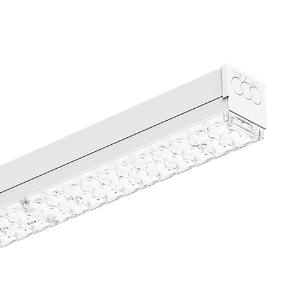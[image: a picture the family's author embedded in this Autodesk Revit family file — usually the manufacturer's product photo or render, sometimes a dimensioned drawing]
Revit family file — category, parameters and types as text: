
# Revit family: 3f_filippi_-_3f_zeta_l_3f_filippi_-_10893_-_3f_zeta_l_30_led_l1194
name_source: partatom
category: Lighting Fixtures
units: mm (PartAtom-declared; Revit-internal decimal feet)

## family parameters
Cut with Voids When Loaded = No
Host = Face
Light Source = No
Part Type = Normal
Room Calculation Point = No
Round Connector Dimension = Use Diameter
Shared = No

## types (1)
- 3F Filippi - 3F Zeta L (1 x LED, 5498 lm, 31 W, 4000 K)
    Apparent Load = 31 VA
    Approval mark = CE
    CIE Flux Codes = 61 95 99 99 100
    Color Rendering = 80
    Color Temperature = 4000 K
    Control Gear = Electronic ballast
    Default Elevation = 1800 mm
    Description = ILLUMINOTECHNICAL
Luminous efficiency 100% (DLOR 99%, ULOR 1%).
Initial luminous flux of the luminaire 5498 lm.
Direct symmetric distribution.
Installation Interdistance Transv.D = 1.39 x hu - Long.D = 1.43 x hu.
Tabular UGR (CIE 117 - 4H-8H; S=0.25H; 70/50/20): RUG 21.7 - 22.4.
Beam angle: 102° - 103°.
Luminous efficacy 177 lm/W.
Lifetime (L93/B10): 30000 h. (tq+25°C)
Lifetime (L90/B10): 50000 h. (tq+25°C)
Lifetime (L85/B10): 80000 h. (tq+25°C)
Lifetime (L80/B10): 100000 h. (tq+25°C)
Sudden decreased luminous flux after 50000 hours: 0% (C0).
Photobiological safety in compliance with IEC/TR 62778: RG0 risk exempt, (IEC 62471).
In compliance with IEC/EN 62722-2-1 - IEC/EN 62717 standards.

SOURCE
Linear LED module 30W/840.
Energy efficiency class (UE 2019/2020 - UE 2019/2015): C.
CIE 13.3 Colour rendering index: CRI >80 (R9 <50%).
IES TM-30 Fidelity Index: Rf = 84 Rg = 95.
CCT nominal colour temperature 4000 K.
Colour initial tolerance (MacAdam): SDCM 3.

MECHANICAL
Housing in hot-galvanised steel, painted in white polyester, obtained through rolling process.
Light unit in hot-galvanised steel, painted in white polyester base with fixing springs and retractable safety hooks in stainless steel.
Lenses for wide distribution, in transparent methacrylate (PMMA) with external flat surface.
End caps in white polycarbonate.
Pair of stainless steel sliding brackets with sliding block screws.
Luminaire with limited surface temperature. - D - (EN 60598-2-24)
Dimensions: 1194x62 mm, height 65 mm. Weight 2.84 kg.
IP40 protection degree.
Mechanical strength to impacts IK06 (1 joule).
Glow-wire test resistance 650°C.

ELECTRICAL
Halogen Free electronic wiring 230V-50/60Hz, power factor 0.90, THD <25%, constant output current, class I, 1 driver.
Power of the luminaire 31 W.
ENEC - CE.
SAFE FLICKER: PstLM=<1 and SVM=<0.4 (IEC TR 61547-1 and IEC TR 63158), to ensure a more comfortable and safe light.
Luminaire compliant with EN 60598-2-22 for power supply from a centralised emergency system CPSS (Central Power Supply System), not incorporated in the luminaire - high risk areas excluded. The default power and flux are 100% in AC and 100% in DC.
Ambient temperature from 0°C to +45°C.
Temperature class T6 max 85°C.
Relative humidity UR: <85%.

INSTALLATION
Ceiling / Suspended / Wall.
All accessories dedicated to this product are available on the Catalog and on our website www.3F-Filippi.com.

APPLICATIONS
Suitable product for food production plants (HACCP), IFS (Food Version 6), BRC (GSFS Food Version 7).
In commercial environments, exhibition areas, shops and stores.

WARNING
Luminaire designed for disposal/recycling at end-of-life.
Replaceable (LED only) light source by a professional. Replaceable control gear by a professional.
    Height = 65 mm
    Lamp = 1 x LED
    Lamp Light Flux = 5498 lm
    Lamp Power = 31 W
    Lamp count = 1
    Length = 1194 mm
    Lifetime = 50000 h
    Luminous efficacy = 177 lm/W
    Manufacturer = 3F Filippi
    ModVariant = No
    Model = 3F Filippi - 10893 - 3F Zeta L 30 LED L1194
    Mounting Place = Ceiling
    Mounting Type = Pendant
    Number of Poles = 1
    OnlyDefault = Yes
    Power Factor = 1
    Product Name = 3F Filippi - 3F Zeta L
    Product group = pendant luminaire
    ProductGroupID = 9
    Protection Class = Protection class I
    Protection Degree = IP 40
    RLX_Detail_Level = 1
    RLX_Emergency_Light_Flux = 0 lm
    RLX_Emergency_Type = 0
    RLX_Emergency_Type_DB = No
    RlxData = <blob elided: 37393 chars, md5=b8651411>
    Socket = socket
    Standby Power = 0 W
    System Light Flux = 5498 lm
    System Power = 31 W
    Type Comments = Product without accessories
    Type Image = 3ffilippi_3f_zeta_l.jpg
    URL = http://relux.com
    VarID = ---
    Voltage = 0 V
    Weight = 0.00 kg
    Width = 62 mm  [stored 0.203412 ft]

note: [stored X ft] marks values corroborated as IEEE doubles in the binary element streams (Revit-internal decimal feet)

## geometry (parser evidence)
native form markers: Blend x4, Sweep x11
no freeform markers — native parametric forms only
